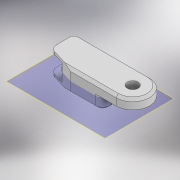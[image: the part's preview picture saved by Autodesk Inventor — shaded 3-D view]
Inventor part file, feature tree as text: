
AUTODESK INVENTOR PART (.ipt)
format: ipt  version: 2022 (Build 260153000, 153)  size: 262,656 bytes
history: native  units: mm
features: extrude x9, sketch x8, projected_geometry x6, fillet x3, chamfer x3, plane x1
ambient origin geometry x8: Origin, YZ Plane, XZ Plane, XY Plane, X Axis, Y Axis, Z Axis, Center Point
bodies: Solid1 (feature_tree)
feature tree (30):
  sketch  "Sketch2"  dims[d0=4.4mm d1=13.5mm]
  extrude  "Extrusion1"  Depth=13.5mm
  extrude  "Extrusion2"  Depth=8.85mm TaperAngle=0.0deg
  extrude  "Extrusion3"  Depth=1.0mm
  extrude  "Extrusion4"  Depth=8.85mm TaperAngle=0.0deg
  extrude  "Extrusion5"  Depth=8.0mm TaperAngle=0.0deg
  extrude  "Extrusion6"  Depth=8.0mm TaperAngle=0.0deg
  extrude  "Extrusion7"  Depth=3.0mm TaperAngle=0.0deg
  sketch  "Sketch8"  dims[d17=10.25mm d18=0.0mm d19=10.25mm d20=0.0mm d21=3.0mm d22=2.0mm d23=2.0mm d24=45.0deg d25=2.0mm d26=2.0mm d27=45.0deg d28=3.0mm]
  fillet  "Fillet1"  Radius=3.0mm
  chamfer  "Chamfer1"  Distance=2.0mm Angle=45.0deg
  chamfer  "Chamfer2"  Distance=2.0mm Angle=45.0deg
  fillet  "Fillet2"  Radius=3.0mm
  sketch  "Sketch9"  dims[d32=3.85mm d33=0.0mm d34=10.0mm d35=0.0mm d36=1.0mm d37=2.0mm d38=45.0deg d39=1.0mm]
  extrude  "Extrusion8"  Depth=10.0mm TaperAngle=0.0deg
  extrude  "Extrusion9"  Depth=1.0mm TaperAngle=45.0deg
  chamfer  "Chamfer4"  Distance=1.0mm
  fillet  "Fillet3"  [1 undecoded]
  plane  "Work Plane1"
  sketch  "Sketch3"  dims[d2=3.85mm d3=0.0mm d4=8.85mm d5=0.0mm]
  projected_geometry  "Projected Loop1"
  sketch  "Sketch4"  dims[d6=0.5mm d7=1.0mm]
  projected_geometry  "Projected Loop2"
  sketch  "Sketch5"  dims[d8=12.5mm d9=8.85mm d10=0.0mm]
  projected_geometry  "Projected Loop3"
  sketch  "Sketch6"  dims[d11=1.0mm d12=8.0mm d13=0.0mm]
  sketch  "Sketch7"  dims[d14=5.1mm d15=8.0mm d16=0.0mm]
  projected_geometry  "Projected Loop5"
  projected_geometry  "Projected Loop6"
  projected_geometry  "Projected Loop7"
note: 1 required parameter value undecoded (feature->parameter linkage not recoverable at this tier; creation-order binding heuristic only, values carry confidence <= 0.55)
